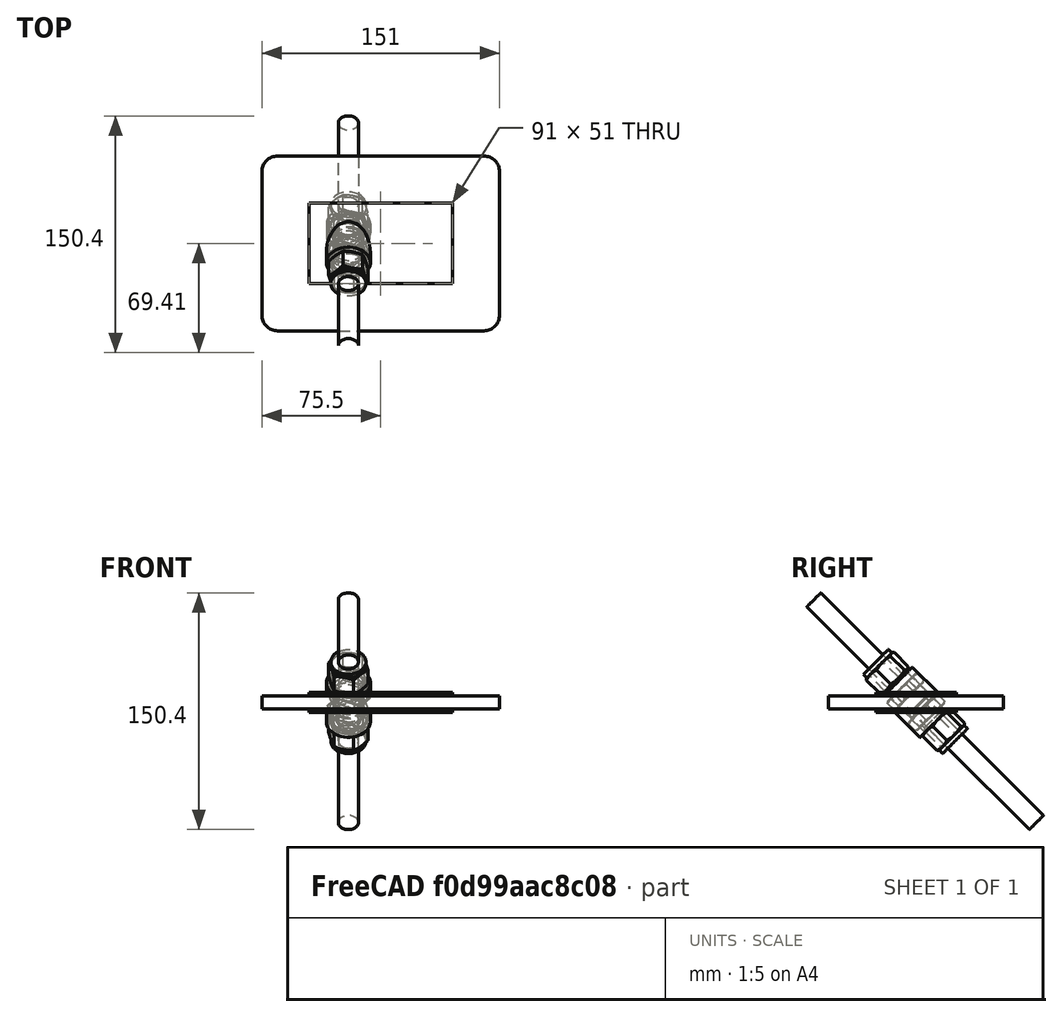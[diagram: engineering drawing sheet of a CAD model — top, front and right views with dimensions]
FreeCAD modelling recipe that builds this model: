
FCSTD DOCUMENT  (FreeCAD 0.20R29410 (Git))
Label: UmbilicalFeedthroughPlateMockup
License: All rights reserved
LicenseURL: http://en.wikipedia.org/wiki/All_rights_reserved
objects: Part::Cylinder×3, Part::Box×2, Part::Fuse×2, Part::Cut×2, Part::Fillet×1, Part::FeaturePython×1, Part::Feature×1
note: 12 computed .brp shape members not serialized (recipe doc carries the construction recipe); baked Part::Feature solids carry a one-line shape summary decoded from their .brp

FEATURE [Part::Box] Box  label="Cube"
  AttacherType = Attacher::AttachEngine3D
  Height = 12.5
  Length = 91
  Width = 51
FEATURE [Part::Box] Box001  label="Cube001"
  AttacherType = Attacher::AttachEngine3D
  Height = 8
  Length = 151
  Placement = pos=(-30,-30,0) rot=(0,0,1;0rad)
  Width = 111
FEATURE [Part::Fillet] Fillet
  Base = -> Box001
  Edges = 4 edges r=10: [Edge1,Edge3,Edge5,Edge7]
  Placement = pos=(0,0,2.25) rot=(0,0,1;0rad)
FEATURE [Part::FeaturePython] Tube  # WARN: FeaturePython — macro-defined, semantics opaque (R4)
  AttacherType = Attacher::AttachEngine3D
  Height = 35
  InnerRadius = 9.53
  OuterRadius = 14
  Placement = pos=(25,38,-6) rot=(1,0,0;0.785398rad)
FEATURE [Part::Feature] Solid  label="PRODUCT_NAME_1"
  Placement = pos=(25,0,32) rot=(0,0.707107,0.707107;1.5708rad)
  shape: bbox 27.5 x 66.09 x 66.09 mm, 125 faces (baked)
FEATURE [Part::Fuse] Fusion
  Base = -> Box
  Tool = -> Fillet
FEATURE [Part::Fuse] Fusion001
  Base = -> Fusion
  Tool = -> Tube
FEATURE [Part::Cylinder] Cylinder
  Angle = 360
  AttacherType = Attacher::AttachEngine3D
  FirstAngle = 0
  Height = 200
  Placement = pos=(25,102,-70) rot=(1,0,0;0.785398rad)
  Radius = 6.35
  SecondAngle = 0
FEATURE [Part::Cylinder] Cylinder001
  Angle = 360
  AttacherType = Attacher::AttachEngine3D
  FirstAngle = 0
  Height = 40
  Placement = pos=(25,38,-6) rot=(1,0,0;0.785398rad)
  Radius = 9.53
  SecondAngle = 0
FEATURE [Part::Cut] Cut
  Base = -> Fusion001
  Tool = -> Cylinder001
FEATURE [Part::Cylinder] Cylinder002
  Angle = 360
  AttacherType = Attacher::AttachEngine3D
  FirstAngle = 0
  Height = 200
  Placement = pos=(25,102,-70) rot=(1,0,0;0.785398rad)
  Radius = 6.35
  SecondAngle = 0
FEATURE [Part::Cut] Cut001
  Base = -> Solid
  Tool = -> Cylinder
